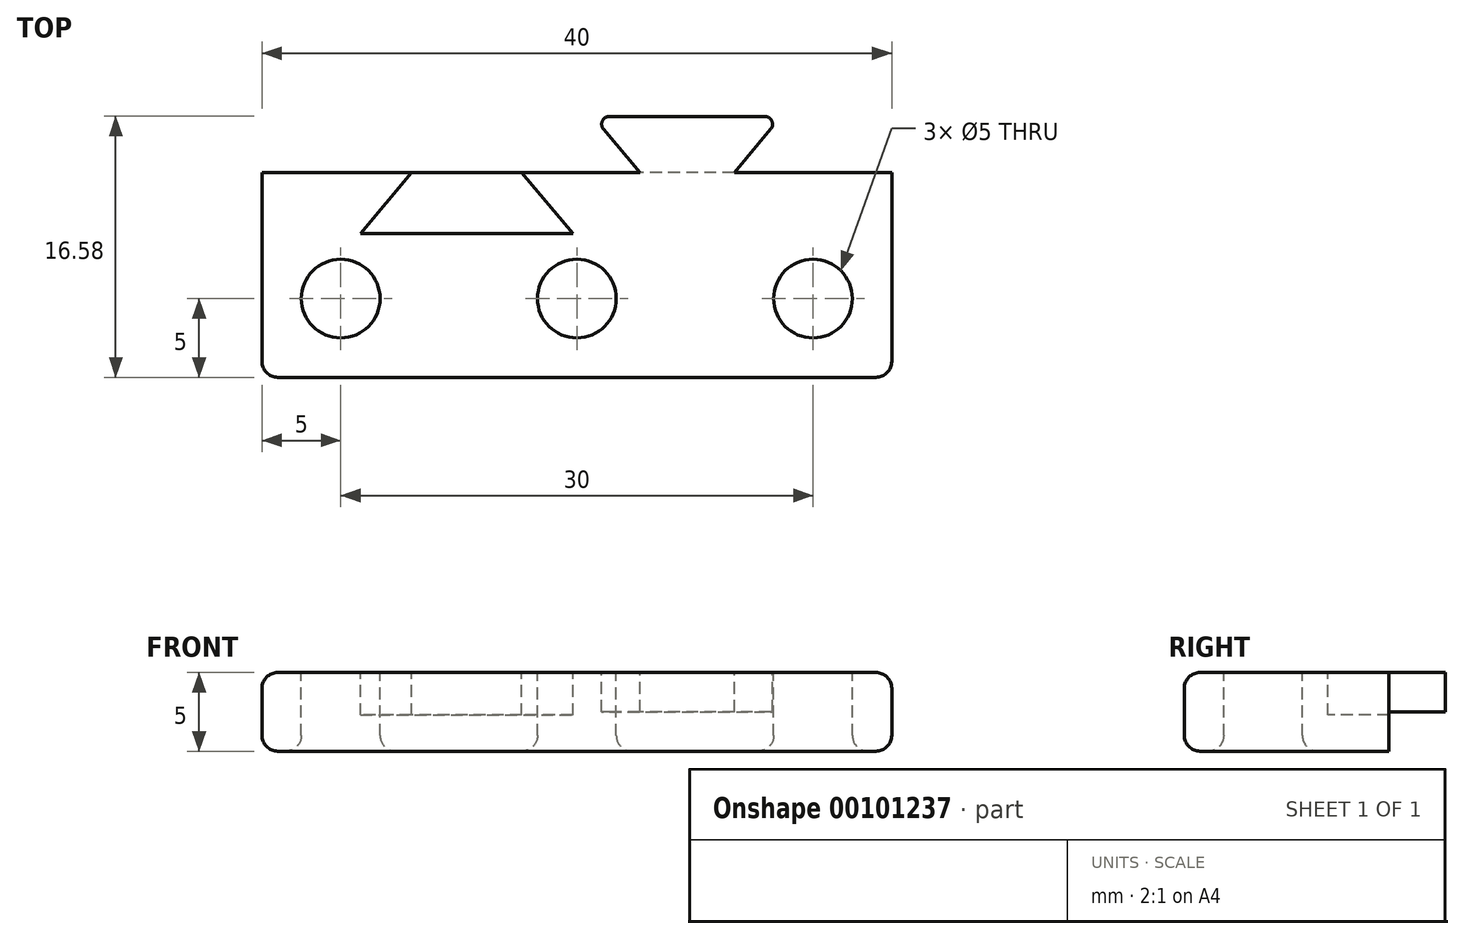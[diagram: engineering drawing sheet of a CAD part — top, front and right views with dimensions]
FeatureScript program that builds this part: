
annotation { "Feature Type Name" : "Feature", "Feature Type Description" : "" }
export const myFeature = defineFeature(function(context is Context, id is Id, definition is map)
    precondition{}
    {
        {
            var Q0;
            Q0=qCreatedBy(makeId("Top.planeOp"),FACE);
            var sketch = newSketch(context, id + "F0", { "sketchPlane" : qUnion([Q0])});
            skLineSegment(sketch, "E0", {"start": v(0, 0) * mm, "end": v(40, 0) * mm});
            skLineSegment(sketch, "E1", {"start": v(40, 0) * mm, "end": v(40, 13) * mm});
            skLineSegment(sketch, "E2", {"start": v(40, 13) * mm, "end": v(0, 13) * mm});
            skLineSegment(sketch, "E3", {"start": v(0, 13) * mm, "end": v(0, 0) * mm});
            skSolve(sketch);
        }
        {
            var Q0;
            Q0=qSketchRegion(id+"F0",true);
            extrude(context, id + "F1", {"entities" : qUnion([Q0]), "depth" : 5 * mm});
        }
        {
            var Q0;
            Q0=makeQuery(id+"F1.opExtrude","CAP_FACE",FACE,{"disambiguationData":[OSD([sQuery(id+"F0.wireOp",EDGE,"E0"),sQuery(id+"F0.wireOp",EDGE,"E1"),sQuery(id+"F0.wireOp",EDGE,"E2"),sQuery(id+"F0.wireOp",EDGE,"E3")])],"isStart":false});
            var sketch = newSketch(context, id + "F2", { "sketchPlane" : qUnion([Q0])});
            skCircle(sketch, "E4", {"center": v(5, 5) * mm, "radius": 2.5 * mm});
            skCircle(sketch, "E5", {"center": v(20, 5) * mm, "radius": 2.5 * mm});
            skCircle(sketch, "E6", {"center": v(35, 5) * mm, "radius": 2.5 * mm});
            skSolve(sketch);
        }
        {
            var Q0;
            Q0=qSketchRegion(id+"F2",true);
            extrude(context, id + "F3", {"entities" : qUnion([Q0]), "operationType" : NewBodyOperationType.REMOVE, "endBound" : BoundingType.THROUGH_ALL, "oppositeDirection" : true, "depth" : 25 * mm});
        }
        {
            var Q0;
            Q0=makeQuery(id+"F1.opExtrude","CAP_FACE",FACE,{"disambiguationData":[OSD([sQuery(id+"F0.wireOp",EDGE,"E0"),sQuery(id+"F0.wireOp",EDGE,"E1"),sQuery(id+"F0.wireOp",EDGE,"E2"),sQuery(id+"F0.wireOp",EDGE,"E3")])],"isStart":false});
            var sketch = newSketch(context, id + "F4", { "sketchPlane" : qUnion([Q0])});
            skLineSegment(sketch, "E7", {"start": v(24, 13) * mm, "end": v(21, 16.58) * mm});
            skLineSegment(sketch, "E8", {"start": v(21, 16.58) * mm, "end": v(33, 16.58) * mm});
            skLineSegment(sketch, "E9", {"start": v(33, 16.58) * mm, "end": v(30, 13) * mm});
            skLineSegment(sketch, "E10", {"start": v(30, 13) * mm, "end": v(24, 13) * mm});
            skSolve(sketch);
        }
        {
            var Q0;
            Q0=qSketchRegion(id+"F4",true);
            extrude(context, id + "F5", {"entities" : qUnion([Q0]), "operationType" : NewBodyOperationType.ADD, "oppositeDirection" : true, "depth" : 2.5 * mm});
        }
        {
            var Q0;
            Q0=makeQuery(id+"F5.boolean.opBoolean","MERGE",FACE,{"derivedFrom":[makeQuery(id+"F1.opExtrude","CAP_FACE",FACE,{"disambiguationData":[OSD([sQuery(id+"F0.wireOp",EDGE,"E0"),sQuery(id+"F0.wireOp",EDGE,"E1"),sQuery(id+"F0.wireOp",EDGE,"E2"),sQuery(id+"F0.wireOp",EDGE,"E3")])],"isStart":false}),makeQuery(id+"F5.opExtrude","CAP_FACE",FACE,{"disambiguationData":[OSD([sQuery(id+"F4.wireOp",EDGE,"E7"),sQuery(id+"F4.wireOp",EDGE,"E8"),sQuery(id+"F4.wireOp",EDGE,"E9"),sQuery(id+"F4.wireOp",EDGE,"E10")])],"isStart":true})]});
            var sketch = newSketch(context, id + "F6", { "sketchPlane" : qUnion([Q0])});
            skLineSegment(sketch, "E11", {"start": v(9.5, 13) * mm, "end": v(6.25, 9.13) * mm});
            skLineSegment(sketch, "E12", {"start": v(6.25, 9.13) * mm, "end": v(19.75, 9.13) * mm});
            skLineSegment(sketch, "E13", {"start": v(19.75, 9.13) * mm, "end": v(16.5, 13) * mm});
            skLineSegment(sketch, "E14", {"start": v(16.5, 13) * mm, "end": v(9.5, 13) * mm});
            skSolve(sketch);
        }
        {
            var Q0;
            Q0=qSketchRegion(id+"F6",true);
            extrude(context, id + "F7", {"entities" : qUnion([Q0]), "operationType" : NewBodyOperationType.REMOVE, "oppositeDirection" : true, "depth" : 2.7 * mm});
        }
        {
            var Q0;
            Q0=makeQuery(id+"F1.opExtrude","SWEPT_EDGE",EDGE,{"disambiguationData":[OSD([sQuery(id+"F0.wireOp",EDGE,"E0"),sQuery(id+"F0.wireOp",EDGE,"E3")])]});
            var Q1;
            Q1=makeQuery(id+"F1.opExtrude","SWEPT_EDGE",EDGE,{"disambiguationData":[OSD([sQuery(id+"F0.wireOp",EDGE,"E0"),sQuery(id+"F0.wireOp",EDGE,"E1")])]});
            var Q2;
            Q2=makeQuery(id+"F1.opExtrude","CAP_EDGE",EDGE,{"disambiguationData":[OSD([sQuery(id+"F0.wireOp",EDGE,"E3")])],"isStart":false});
            var Q3;
            Q3=makeQuery(id+"F1.opExtrude","CAP_EDGE",EDGE,{"disambiguationData":[OSD([sQuery(id+"F0.wireOp",EDGE,"E3")])],"isStart":true});
            var Q4;
            Q4=makeQuery(id+"F1.opExtrude","CAP_EDGE",EDGE,{"disambiguationData":[OSD([sQuery(id+"F0.wireOp",EDGE,"E1")])],"isStart":false});
            var Q5;
            Q5=makeQuery(id+"F1.opExtrude","CAP_EDGE",EDGE,{"disambiguationData":[OSD([sQuery(id+"F0.wireOp",EDGE,"E1")])],"isStart":true});
            var Q6;
            Q6=makeQuery(id+"F1.opExtrude","CAP_EDGE",EDGE,{"disambiguationData":[OSD([sQuery(id+"F0.wireOp",EDGE,"E0")])],"isStart":false});
            var Q7;
            Q7=makeQuery(id+"F1.opExtrude","CAP_EDGE",EDGE,{"disambiguationData":[OSD([sQuery(id+"F0.wireOp",EDGE,"E0")])],"isStart":true});
            fillet(context, id + "F8", {"entities" : qUnion([Q0, Q1, Q2, Q3, Q4, Q5, Q6, Q7]), "radius" : 1 * mm, "tangentPropagation" : true, "allowEdgeOverflow" : false});
        }
        {
            var Q0;
            Q0=makeQuery(id+"F3.boolean.opBoolean","COPY",EDGE,{"derivedFrom":makeQuery(id+"F3.opExtrude","CAP_EDGE",EDGE,{"disambiguationData":[OSD([sQuery(id+"F2.wireOp",EDGE,"E4")])],"isStart":true})});
            var Q1;
            Q1=makeQuery(id+"F3.boolean.opBoolean","COPY",EDGE,{"derivedFrom":makeQuery(id+"F3.opExtrude","CAP_EDGE",EDGE,{"disambiguationData":[OSD([sQuery(id+"F2.wireOp",EDGE,"E5")])],"isStart":true})});
            var Q2;
            Q2=makeQuery(id+"F3.boolean.opBoolean","COPY",EDGE,{"derivedFrom":makeQuery(id+"F3.opExtrude","CAP_EDGE",EDGE,{"disambiguationData":[OSD([sQuery(id+"F2.wireOp",EDGE,"E6")])],"isStart":true})});
            var Q3;
            Q3=makeQuery(id+"F3.boolean.opBoolean","INTERSECT",EDGE,{"derivedFrom":[makeQuery(id+"F1.opExtrude","CAP_FACE",FACE,{"disambiguationData":[OSD([sQuery(id+"F0.wireOp",EDGE,"E0"),sQuery(id+"F0.wireOp",EDGE,"E1"),sQuery(id+"F0.wireOp",EDGE,"E2"),sQuery(id+"F0.wireOp",EDGE,"E3")])],"isStart":true}),makeQuery(id+"F3.opExtrude","SWEPT_FACE",FACE,{"disambiguationData":[OSD([sQuery(id+"F2.wireOp",EDGE,"E4")])]})]});
            var Q4;
            Q4=makeQuery(id+"F3.boolean.opBoolean","INTERSECT",EDGE,{"derivedFrom":[makeQuery(id+"F1.opExtrude","CAP_FACE",FACE,{"disambiguationData":[OSD([sQuery(id+"F0.wireOp",EDGE,"E0"),sQuery(id+"F0.wireOp",EDGE,"E1"),sQuery(id+"F0.wireOp",EDGE,"E2"),sQuery(id+"F0.wireOp",EDGE,"E3")])],"isStart":true}),makeQuery(id+"F3.opExtrude","SWEPT_FACE",FACE,{"disambiguationData":[OSD([sQuery(id+"F2.wireOp",EDGE,"E5")])]})]});
            var Q5;
            Q5=makeQuery(id+"F3.boolean.opBoolean","INTERSECT",EDGE,{"derivedFrom":[makeQuery(id+"F1.opExtrude","CAP_FACE",FACE,{"disambiguationData":[OSD([sQuery(id+"F0.wireOp",EDGE,"E0"),sQuery(id+"F0.wireOp",EDGE,"E1"),sQuery(id+"F0.wireOp",EDGE,"E2"),sQuery(id+"F0.wireOp",EDGE,"E3")])],"isStart":true}),makeQuery(id+"F3.opExtrude","SWEPT_FACE",FACE,{"disambiguationData":[OSD([sQuery(id+"F2.wireOp",EDGE,"E6")])]})]});
            fillet(context, id + "F9", {"entities" : qUnion([Q0, Q1, Q2, Q3, Q4, Q5]), "radius" : 1 * mm, "tangentPropagation" : true, "allowEdgeOverflow" : false});
        }
        {
            var Q0;
            Q0=makeQuery(id+"F5.opExtrude","SWEPT_EDGE",EDGE,{"disambiguationData":[OSD([sQuery(id+"F4.wireOp",EDGE,"E7"),sQuery(id+"F4.wireOp",EDGE,"E8")])]});
            var Q1;
            Q1=makeQuery(id+"F5.opExtrude","SWEPT_EDGE",EDGE,{"disambiguationData":[OSD([sQuery(id+"F4.wireOp",EDGE,"E8"),sQuery(id+"F4.wireOp",EDGE,"E9")])]});
            var Q2;
            Q2=makeQuery(id+"F7.boolean.opBoolean","COPY",EDGE,{"derivedFrom":makeQuery(id+"F7.opExtrude","SWEPT_EDGE",EDGE,{"disambiguationData":[OSD([sQuery(id+"F0.wireOp",EDGE,"E2"),sQuery(id+"F6.wireOp",EDGE,"E11"),sQuery(id+"F6.wireOp",EDGE,"E14")])]})});
            var Q3;
            Q3=makeQuery(id+"F7.boolean.opBoolean","COPY",EDGE,{"derivedFrom":makeQuery(id+"F7.opExtrude","SWEPT_EDGE",EDGE,{"disambiguationData":[OSD([sQuery(id+"F0.wireOp",EDGE,"E2"),sQuery(id+"F6.wireOp",EDGE,"E13"),sQuery(id+"F6.wireOp",EDGE,"E14")])]})});
            fillet(context, id + "F10", {"entities" : qUnion([Q0, Q1, Q2, Q3]), "radius" : 0.5 * mm, "tangentPropagation" : true, "allowEdgeOverflow" : false});
        }
    });
